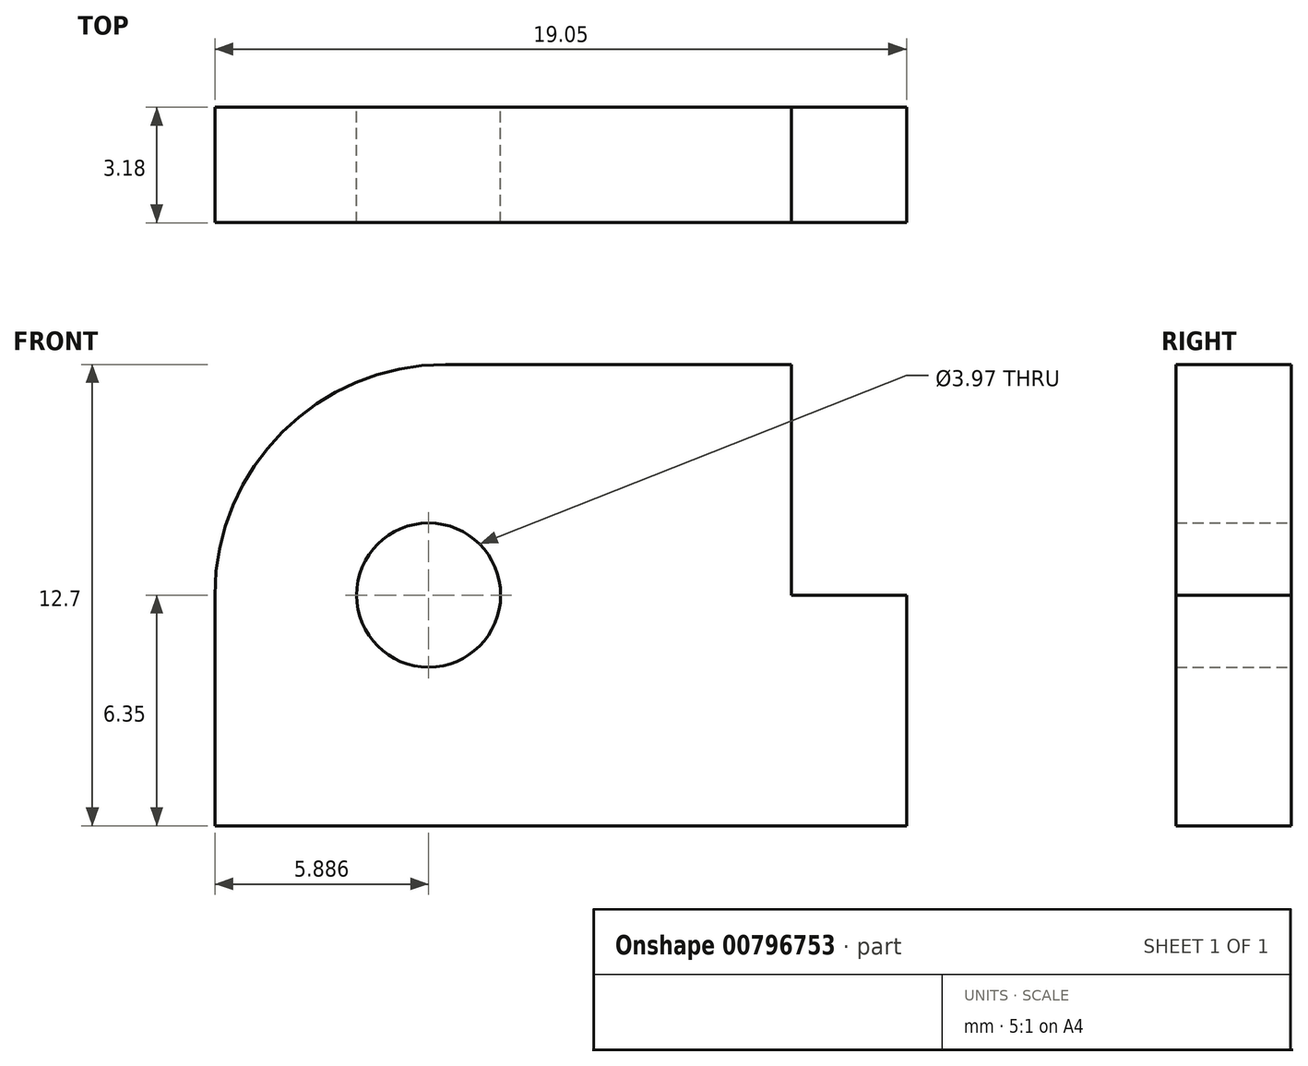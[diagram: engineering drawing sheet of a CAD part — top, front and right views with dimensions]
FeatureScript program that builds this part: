
annotation { "Feature Type Name" : "Feature", "Feature Type Description" : "" }
export const myFeature = defineFeature(function(context is Context, id is Id, definition is map)
    precondition{}
    {
        {
            var Q0;
            Q0=qCreatedBy(makeId("Front.planeOp"),FACE);
            var sketch = newSketch(context, id + "F0", { "sketchPlane" : qUnion([Q0])});
            skLineSegment(sketch, "E0.bottom", {"start": v(0, 0) * mm, "end": v(19.05, 0) * mm});
            skLineSegment(sketch, "E0.top", {"start": v(6.35, 12.7) * mm, "end": v(15.88, 12.7) * mm});
            skLineSegment(sketch, "E0.left", {"start": v(0, 0) * mm, "end": v(0, 6.35) * mm});
            skLineSegment(sketch, "E0.right", {"start": v(19.05, 0) * mm, "end": v(19.05, 6.35) * mm});
            skLineSegment(sketch, "E1", {"start": v(5.89, 12.7) * mm, "end": v(5.89, 0) * mm, "construction": true});
            skPoint(sketch, "E2", {"position": v(5.89, 6.35) * mm});
            skCircle(sketch, "E3", {"center": v(5.89, 6.35) * mm, "radius": 1.98 * mm});
            skPoint(sketch, "E4.visualSharp", {"position": v(0, 12.7) * mm});
            skArc(sketch, "E4.filletArc", {"start": v(6.35, 12.7) * mm, "mid": v(1.86, 10.84) * mm, "end": v(0, 6.35) * mm});
            skLineSegment(sketch, "E5.top", {"start": v(19.05, 6.35) * mm, "end": v(15.88, 6.35) * mm});
            skLineSegment(sketch, "E5.right", {"start": v(15.88, 12.7) * mm, "end": v(15.88, 6.35) * mm});
            skSolve(sketch);
        }
        {
            var Q0;
            Q0=makeQuery(id+"F0.imprint","IMPRINT",FACE,{"disambiguationData":[TD([[makeQuery(id+"F0.imprint","IMPRINT",EDGE,{"derivedFrom":sQuery(id+"F0.wireOp",EDGE,"E0.bottom")}),1.0]])]});
            extrude(context, id + "F1", {"entities" : qUnion([Q0]), "depth" : 3.17 * mm, "offsetDistance" : 25.4 * mm});
        }
    });
